# Revit family: 4M_Strainer_UNIVAL_STR-0201 - 15-450 mm
name_source: partatom
category: Pipe Accessories
revit_build: Autodesk Revit 2016 (Build: 20150220_1215(x64)
units: mm (PartAtom-declared; Revit-internal decimal feet)

## family parameters
Always vertical = Yes
Cut with Voids When Loaded = No
OmniClass Number = 23.65.55.14
OmniClass Title = Valves for Liquid Services
Part Type = Valve - Breaks Into
Round Connector Dimension = Use Diameter
Shared = No
Work Plane-Based = No

## types (17) — shared parameters
Angle = 45.00°
Body Material = Cast iron
Certifications = TSE, EAC, CE
Colour = UNIVAL_IRON
Connection Type = Flanged
Description = Strainer
Description TR = Pislik tutucu
Loss Method = Not Defined
Manufacturer = Giacomini Unival
Giacomini Unival
Giacomini Unival
Max. Working Temperature = 250°C
Pressure Rating = PN16
Standard No = TS 11494
URL = http://www.unival.com.tr

## per-type parameters (varying)
| type | 1st_pipe_center_dist | 1st_pipe_dist | 1st_pipe_l | 2nd_pipe_l | Body_Do | Body_rd | DN | Flange Size | Flange_w | H | L | Model | Plate_W | Plate_d | RectangleExtr | Y_curve | Ypipe_L | Ypipe_r |
| DN125 | 25 mm  [stored 0.082021 ft] | 50 mm  [stored 0.164042 ft] | 274 mm | 135 mm | 150 mm | 75 mm | 125 mm | M_Flange - 15-450 mm : DN125 | 17 mm | 240 mm | 400 mm | STR-0201X125 | 150 mm | 13 mm  [stored 0.0426509 ft] | 71 mm | 220 mm | 216 mm | 70 mm |
| DN65 | 15 mm  [stored 0.0492126 ft] | 30 mm  [stored 0.0984252 ft] | 200 mm | 87 mm | 90 mm | 45 mm | 65 mm | M_Flange - 15-450 mm : DN65 | 17 mm | 156 mm | 290 mm | STR-0201X065 | 98 mm | 7 mm  [stored 0.0229659 ft] | 43 mm  [stored 0.141076 ft] | 120 mm | 147 mm | 42 mm |
| DN50 | 13 mm  [stored 0.0426509 ft] | 25 mm  [stored 0.082021 ft] | 144 mm | 77 mm | 75 mm | 38 mm  [stored 0.124672 ft] | 50 mm | M_Flange - 15-450 mm : DN50 | 17 mm | 130 mm | 230 mm | STR-0201X050 | 75 mm | 5 mm  [stored 0.0164042 ft] | 36 mm | 120 mm | 122 mm | 35 mm  [stored 0.114829 ft] |
| DN150 | 29 mm  [stored 0.0951444 ft] | 58 mm | 352 mm | 153 mm | 175 mm | 88 mm | 150 mm | M_Flange - 15-450 mm : DN150 | 17 mm | 282 mm | 480 mm | STR-0201X150 | 225 mm | 15 mm  [stored 0.0492126 ft] | 83 mm | 280 mm | 255 mm | 81 mm |
| DN200 | 38 mm  [stored 0.124672 ft] | 75 mm | 445 mm | 194 mm | 225 mm | 113 mm | 200 mm | M_Flange - 15-450 mm : DN200 | 18 mm  [stored 0.0590551 ft] | 335 mm | 600 mm | STR-0201X200 | 300 mm | 20 mm  [stored 0.0656168 ft] | 107 mm | 300 mm | 289 mm | 105 mm |
| DN250 | 46 mm | 92 mm | 545 mm | 237 mm | 275 mm | 138 mm | 250 mm | M_Flange - 15-450 mm : DN250 | 20 mm  [stored 0.0656168 ft] | 460 mm | 730 mm | STR-0201X250 | 375 mm | 25 mm  [stored 0.082021 ft] | 131 mm | 320 mm | 425 mm | 128 mm |
| DN300 | 54 mm | 108 mm | 637 mm | 277 mm | 325 mm | 163 mm | 300 mm | M_Flange - 15-450 mm : DN300 | 23 mm  [stored 0.0754593 ft] | 515 mm | 850 mm | STR-0201X300 | 450 mm | 30 mm  [stored 0.0984252 ft] | 155 mm | 500 mm | 461 mm | 151 mm |
| DN80 | 18 mm  [stored 0.0590551 ft] | 35 mm  [stored 0.114829 ft] | 217 mm | 94 mm | 105 mm | 53 mm  [stored 0.173885 ft] | 80 mm | M_Flange - 15-450 mm : DN80 | 17 mm | 172 mm | 310 mm | STR-0201X080 | 120 mm | 8 mm  [stored 0.0262467 ft] | 50 mm  [stored 0.164042 ft] | 150 mm | 157 mm | 49 mm |
| DN100 | 21 mm | 42 mm | 250 mm | 108 mm | 125 mm | 63 mm | 100 mm | M_Flange - 15-450 mm : DN100 | 17 mm | 215 mm | 350 mm | STR-0201X100 | 150 mm | 10 mm  [stored 0.0328084 ft] | 60 mm | 220 mm | 201 mm | 58 mm |
| DN350 | 63 mm | 125 mm | 807 mm | 245 mm | 375 mm | 188 mm | 350 mm | M_Flange - 15-450 mm : DN350 | 27 mm | 755 mm | 980 mm | STR-0201X350 | 480 mm | 35 mm  [stored 0.114829 ft] | 179 mm | 1050 mm | 760 mm | 174 mm |
| DN400 | 71 mm | 142 mm | 900 mm | 286 mm | 425 mm | 213 mm | 400 mm | M_Flange - 15-450 mm : DN400 | 28 mm  [stored 0.0918635 ft] | 827 mm | 1100 mm | STR-0201X400 | 550 mm | 40 mm  [stored 0.131234 ft] | 202 mm | 1000 mm | 820 mm | 198 mm |
| DN450 | 79 mm | 158 mm | 998 mm | 300 mm | 475 mm | 238 mm | 450 mm | M_Flange - 15-450 mm : DN450 | 30 mm  [stored 0.0984252 ft] | 930 mm | 1200 mm | STR-0201X450 | 551 mm | 45 mm | 226 mm | 800 mm | 925 mm | 221 mm |
| DN40 | 11 mm  [stored 0.0360892 ft] | 22 mm | 122 mm | 66 mm | 65 mm | 33 mm  [stored 0.108268 ft] | 40 mm | M_Flange - 15-450 mm : DN40 | 17 mm | 118 mm | 200 mm | STR-0201X040 | 60 mm | 4 mm  [stored 0.0131234 ft] | 31 mm | 100 mm | 113 mm | 30 mm  [stored 0.0984252 ft] |
| DN32 | 10 mm  [stored 0.0328084 ft] | 19 mm | 99 mm | 66 mm | 57 mm  [stored 0.187008 ft] | 29 mm  [stored 0.0951444 ft] | 32 mm | M_Flange - 15-450 mm : DN32 | 17 mm | 111 mm | 180 mm | STR-0201X032 | 48 mm  [stored 0.15748 ft] | 3 mm  [stored 0.00984252 ft] | 27 mm | 90 mm | 110 mm | 27 mm |
| DN25 | 8 mm  [stored 0.0262467 ft] | 17 mm | 73 mm | 70 mm | 50 mm  [stored 0.164042 ft] | 25 mm  [stored 0.082021 ft] | 25 mm | M_Flange - 15-450 mm : DN25 | 17 mm | 91 mm | 160 mm | STR-0201X025 | 38 mm  [stored 0.124672 ft] | 3 mm  [stored 0.00984252 ft] | 24 mm  [stored 0.0787402 ft] | 120 mm | 88 mm | 23 mm  [stored 0.0754593 ft] |
| DN20 | 8 mm  [stored 0.0262467 ft] | 15 mm  [stored 0.0492126 ft] | 75 mm | 56 mm  [stored 0.183727 ft] | 45 mm | 23 mm  [stored 0.0754593 ft] | 20 mm | M_Flange - 15-450 mm : DN20 | 17 mm | 83 mm | 150 mm | STR-0201X020 | 50 mm  [stored 0.164042 ft] | 2 mm  [stored 0.00656168 ft] | 21 mm | 70 mm | 80 mm | 21 mm |
| DN15 | 7 mm  [stored 0.0229659 ft] | 13 mm  [stored 0.0426509 ft] | 53 mm  [stored 0.173885 ft] | 56 mm  [stored 0.183727 ft] | 40 mm  [stored 0.131234 ft] | 20 mm  [stored 0.0656168 ft] | 15 mm | M_Flange - 15-450 mm : DN15 | 17 mm | 76 mm | 130 mm | STR-0201X015 | 50 mm  [stored 0.164042 ft] | 2 mm  [stored 0.00656168 ft] | 19 mm | 60 mm | 75 mm | 19 mm |

note: [stored X ft] marks values corroborated as IEEE doubles in the binary element streams (Revit-internal decimal feet)

## geometry (parser evidence)
native form markers: Sweep x8
no freeform markers — native parametric forms only
